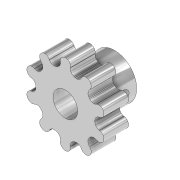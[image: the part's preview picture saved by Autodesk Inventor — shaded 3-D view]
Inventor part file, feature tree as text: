
AUTODESK INVENTOR PART (.ipt)
format: ipt  version: 2020 (Build 240168000, 168)  size: 233,472 bytes
history: native  units: in
note: dims shown in document units (in); Inventor stores cm internally (conversion verified against a paired STEP export)
features: extrude x3, sketch x3
ambient origin geometry x8: Origin, YZ Plane, XZ Plane, XY Plane, X Axis, Y Axis, Z Axis, Center Point
bodies: Body1 (feature_tree)
feature tree (6):
  extrude  "Extrusion4"  Depth=0.1969in
  extrude  "Extrusion5"  Depth=0.0866in
  extrude  "Extrusion6"  Depth=0.1969in
  sketch  "Sketch4"  dims[d1=0.563in d2=0.0866in d19=0.1969in]
  sketch  "Sketch5"  dims[d20=0.6457in d21=0.0866in]
  sketch  "Sketch6"  dims[d22=0.0827in d23=0.0827in d24=0.0827in d25=3.937in d27=360.0deg d29=0.1969in d30=0.0in d31=0.0787in d32=0.1969in d33=0.0in d34=0.0748in d35=0.1969in d36=0.0in]
